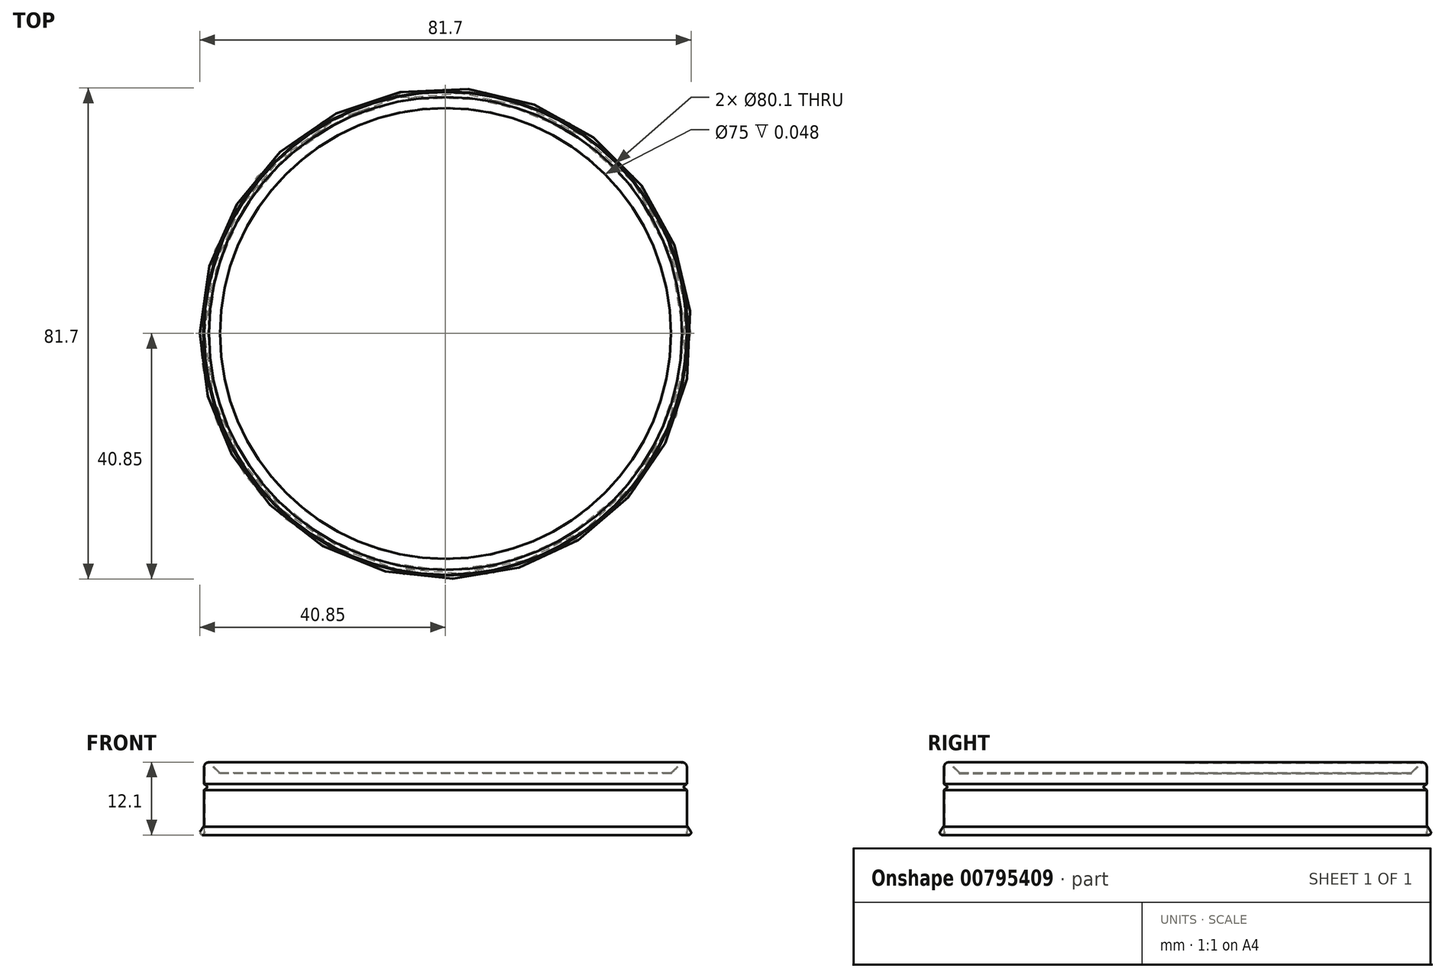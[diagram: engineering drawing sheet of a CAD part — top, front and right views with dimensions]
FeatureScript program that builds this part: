
annotation { "Feature Type Name" : "Feature", "Feature Type Description" : "" }
export const myFeature = defineFeature(function(context is Context, id is Id, definition is map)
    precondition{}
    {
        {
            var Q0;
            Q0=qCreatedBy(makeId("Top.planeOp"),FACE);
            var sketch = newSketch(context, id + "F0", { "sketchPlane" : qUnion([Q0])});
            skCircle(sketch, "E0", {"center": v(0, 0) * mm, "radius": 40.15 * mm});
            skSolve(sketch);
        }
        {
            var Q0;
            Q0 = qSketchRegion(id + "F0", true);
            extrude(context, id + "F1", {"entities" : qUnion([Q0]), "depth" : 11.7 * mm, "offsetDistance" : 25 * mm});
        }
        {
            var Q0;
            Q0=makeQuery(id+"F1.opExtrude","CAP_EDGE",EDGE,{"disambiguationData":[OSD([sQuery(id+"F0.wireOp",EDGE,"E0")])],"isStart":false});
            fillet(context, id + "F2", {"entities" : qUnion([Q0]), "radius" : .8 * mm, "tangentPropagation" : true, "allowEdgeOverflow" : false});
        }
        {
            var Q0;
            Q0=qCreatedBy(makeId("Front.planeOp"),FACE);
            var sketch = newSketch(context, id + "F3", { "sketchPlane" : qUnion([Q0])});
            skLineSegment(sketch, "E1", {"start": v(-40.15, 8.1) * mm, "end": v(-39.5, 7.6) * mm});
            skLineSegment(sketch, "E2", {"start": v(-39.5, 7.6) * mm, "end": v(-40.15, 7.1) * mm});
            skLineSegment(sketch, "E3", {"start": v(-40.15, 7.1) * mm, "end": v(-40.15, 8.1) * mm});
            skSolve(sketch);
        }
        {
            var Q0;
            Q0 = qSketchRegion(id + "F3", true);
            var Q1;
            Q1=makeQuery(id+"F2.opFillet","BLEND_FACE",FACE,{"disambiguationData":[OSD([sQuery(id+"F0.wireOp",EDGE,"E0")])]});
            revolve(context, id + "F4", {"operationType" : NewBodyOperationType.REMOVE, "surfaceOperationType" : NewSurfaceOperationType.NEW, "entities" : qUnion([Q0]), "axis" : qUnion([Q1]), "revolveType" : RevolveType.FULL, "oppositeDirection" : true});
        }
        {
            var Q0;
            Q0=makeQuery(id+"F1.opExtrude","CAP_FACE",FACE,{"disambiguationData":[OSD([sQuery(id+"F0.wireOp",EDGE,"E0")])],"isStart":false});
            var sketch = newSketch(context, id + "F5", { "sketchPlane" : qUnion([Q0])});
            skCircle(sketch, "E4", {"center": v(0, 0) * mm, "radius": 37.5 * mm});
            skSolve(sketch);
        }
        {
            var Q0;
            Q0 = qSketchRegion(id + "F5", true);
            extrude(context, id + "F6", {"entities" : qUnion([Q0]), "operationType" : NewBodyOperationType.REMOVE, "oppositeDirection" : true, "depth" : 1.8 * mm, "offsetDistance" : 25 * mm});
        }
        {
            var Q0;
            Q0=qCreatedBy(makeId("Front.planeOp"),FACE);
            var sketch = newSketch(context, id + "F7", { "sketchPlane" : qUnion([Q0])});
            skLineSegment(sketch, "E5", {"start": v(-39.35, 11.7) * mm, "end": v(-37.45, 11.7) * mm});
            skLineSegment(sketch, "E6", {"start": v(-37.45, 11.7) * mm, "end": v(-37.45, 9.9) * mm});
            skLineSegment(sketch, "E7", {"start": v(-37.45, 9.9) * mm, "end": v(-39.35, 11.7) * mm});
            skSolve(sketch);
        }
        {
            var Q0;
            Q0 = qSketchRegion(id + "F7", true);
            var Q1;
            {var subQ0=sQuery(id+"F0.wireOp",EDGE,"E0");Q1=makeQuery(id+"F2.opFillet","BLEND_EDGE",EDGE,{"blendedFrom":[makeQuery(id+"F1.opExtrude","CAP_EDGE",EDGE,{"disambiguationData":[OSD([subQ0])],"isStart":false}),makeQuery(id+"F1.opExtrude","CAP_FACE",FACE,{"disambiguationData":[OSD([subQ0])],"isStart":false})],"blendedInto":[makeQuery(id+"F1.opExtrude","CAP_FACE",FACE,{"disambiguationData":[OSD([subQ0])],"isStart":false})]});}
            revolve(context, id + "F8", {"operationType" : NewBodyOperationType.REMOVE, "surfaceOperationType" : NewSurfaceOperationType.NEW, "entities" : qUnion([Q0]), "axis" : qUnion([Q1]), "revolveType" : RevolveType.FULL, "oppositeDirection" : true});
        }
        {
            var Q0;
            Q0=makeQuery(id+"F1.opExtrude","CAP_FACE",FACE,{"disambiguationData":[OSD([sQuery(id+"F0.wireOp",EDGE,"E0")])],"isStart":true});
            shell(context, id + "F9", {"entities" : qUnion([Q0]), "thickness" : .1 * mm});
        }
        {
            var Q0;
            Q0=makeQuery(id+"F9.opShell","OFFSET_EDGE",EDGE,{"disambiguationData":[OSD([sQuery(id+"F3.wireOp",EDGE,"E1"),sQuery(id+"F3.wireOp",EDGE,"E2")])]});
            var Q1;
            Q1=makeQuery(id+"F9.opShell","OFFSET_EDGE",EDGE,{"disambiguationData":[OSD([sQuery(id+"F3.wireOp",EDGE,"E1"),sQuery(id+"F3.wireOp",EDGE,"E3")])]});
            fillet(context, id + "F10", {"entities" : qUnion([Q0, Q1]), "radius" : .25 * mm, "tangentPropagation" : true, "allowEdgeOverflow" : false});
        }
        {
            var Q0;
            Q0=qCreatedBy(makeId("Front.planeOp"),FACE);
            var sketch = newSketch(context, id + "F11", { "sketchPlane" : qUnion([Q0])});
            skArc(sketch, "E8", {"start": v(-40.78, 0.22) * mm, "mid": v(-40.56, -0.38) * mm, "end": v(-40.05, 0) * mm});
            skArc(sketch, "E9", {"start": v(-40.7, 0.16) * mm, "mid": v(-40.54, -0.29) * mm, "end": v(-40.15, 0) * mm});
            skLineSegment(sketch, "E10", {"start": v(-40.7, 0.16) * mm, "end": v(-40.2, 0.93) * mm});
            skLineSegment(sketch, "E11", {"start": v(-40.2, 0.93) * mm, "end": v(-40.28, 0.99) * mm});
            skLineSegment(sketch, "E12", {"start": v(-40.28, 0.99) * mm, "end": v(-40.78, 0.22) * mm});
            skLineSegment(sketch, "E13", {"start": v(-40.15, 0) * mm, "end": v(-40.05, 0) * mm});
            skSolve(sketch);
        }
        {
            var Q0;
            Q0 = qSketchRegion(id + "F11", true);
            var Q1;
            {var subQ0=sQuery(id+"F0.wireOp",EDGE,"E0");Q1=makeQuery(id+"F2.opFillet","BLEND_EDGE",EDGE,{"blendedFrom":[makeQuery(id+"F1.opExtrude","CAP_EDGE",EDGE,{"disambiguationData":[OSD([subQ0])],"isStart":false}),makeQuery(id+"F1.opExtrude","CAP_FACE",FACE,{"disambiguationData":[OSD([subQ0])],"isStart":false})],"blendedInto":[makeQuery(id+"F1.opExtrude","CAP_FACE",FACE,{"disambiguationData":[OSD([subQ0])],"isStart":false})]});}
            revolve(context, id + "F12", {"operationType" : NewBodyOperationType.ADD, "surfaceOperationType" : NewSurfaceOperationType.NEW, "entities" : qUnion([Q0]), "axis" : qUnion([Q1]), "revolveType" : RevolveType.FULL});
        }
        {
            var Q0;
            Q0=makeQuery(id+"F4.boolean.opBoolean","COPY",EDGE,{"derivedFrom":makeQuery(id+"F4.opRevolve","SWEPT_EDGE",EDGE,{"disambiguationData":[OSD([sQuery(id+"F3.wireOp",EDGE,"E1"),sQuery(id+"F3.wireOp",EDGE,"E2")])]})});
            fillet(context, id + "F13", {"entities" : qUnion([Q0]), "radius" : .2 * mm, "tangentPropagation" : true, "allowEdgeOverflow" : false});
        }
    });
